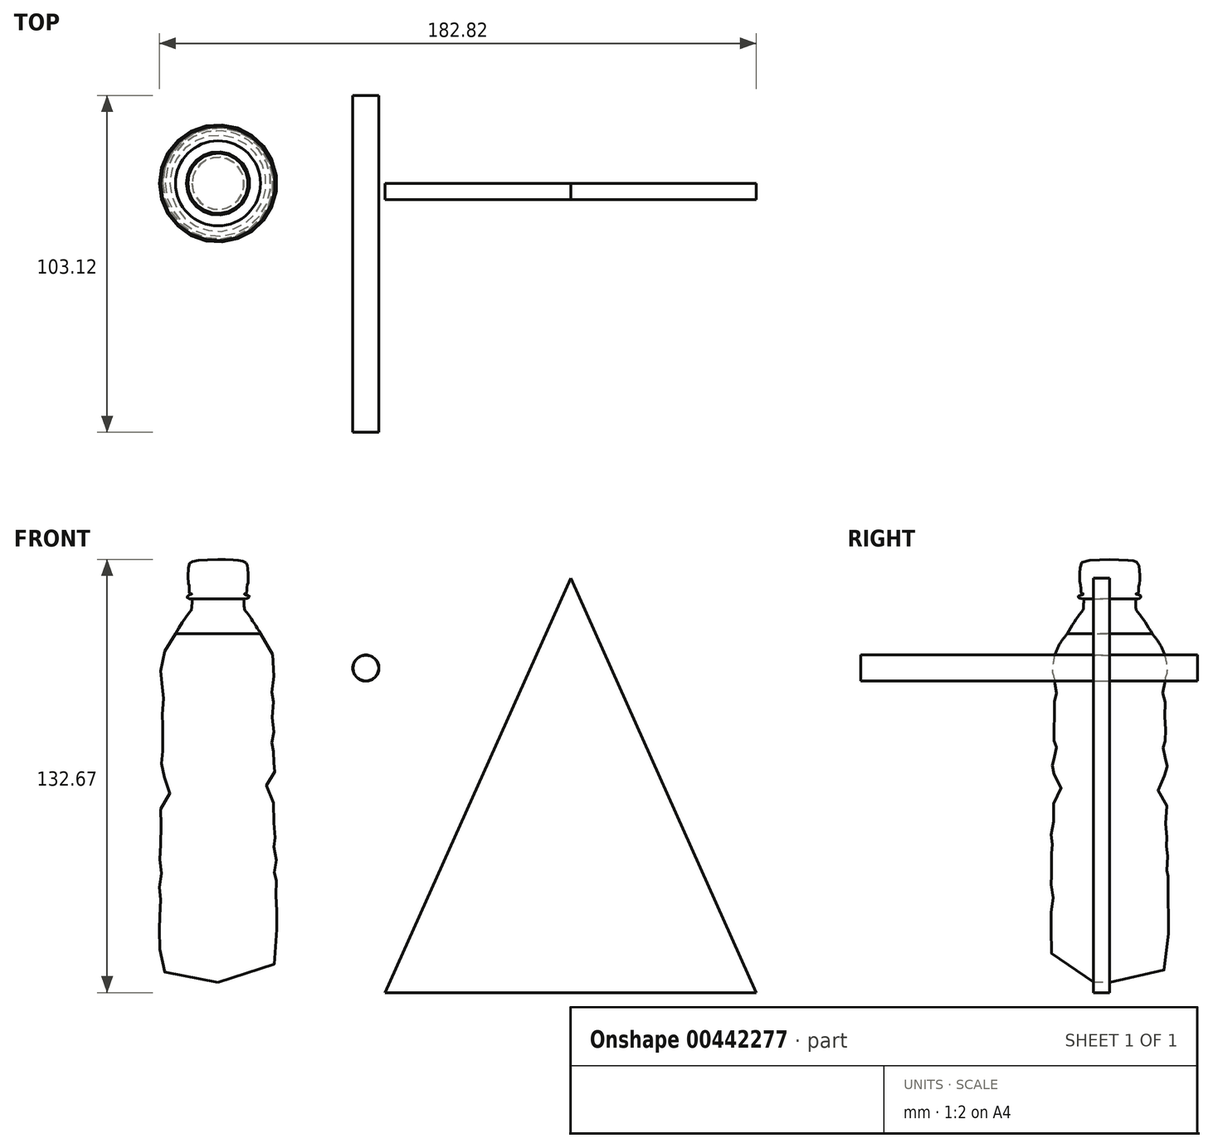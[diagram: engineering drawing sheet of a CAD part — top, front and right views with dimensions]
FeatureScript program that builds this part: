
annotation { "Feature Type Name" : "Feature", "Feature Type Description" : "" }
export const myFeature = defineFeature(function(context is Context, id is Id, definition is map)
    precondition{}
    {
        {
            var Q0;
            Q0=qCreatedBy(makeId("Front.planeOp"),FACE);
            var sketch = newSketch(context, id + "F0", { "sketchPlane" : qUnion([Q0])});
            skLineSegment(sketch, "E0", {"start": v(-25.2, -72.37) * mm, "end": v(-25.2, 34.47) * mm});
            skPoint(sketch, "E0.startSnap0", {"position": v(-25.2, -77.68) * mm});
            skLineSegment(sketch, "E1", {"start": v(-25.2, 34.47) * mm, "end": v(-38.23, 34.47) * mm});
            skFitSpline(sketch, "E2", {"points": [v(-38.23, 34.47) * mm, v(-39.29, 33.05) * mm, v(-40.03, 32.06) * mm, v(-41.03, 30.36) * mm, v(-41.81, 28.4) * mm, v(-42.22, 27.1) * mm, v(-42.63, 24.63) * mm, v(-42.75, 23.45) * mm, v(-42.66, 22.2) * mm, v(-42.19, 20.87) * mm, v(-42.19, 19.83) * mm, v(-42.21, 18.8) * mm, v(-42.22, 18.02) * mm, v(-42.18, 17.28) * mm, v(-41.85, 16.73) * mm, v(-41.48, 16.36) * mm, v(-41.4, 15.76) * mm, v(-41.53, 15.28) * mm, v(-41.82, 14.68) * mm, v(-42.06, 14.12) * mm, v(-42.26, 12.97) * mm, v(-42.27, 11.72) * mm, v(-42.26, 10.27) * mm, v(-42.17, 9.37) * mm, v(-41.66, 8.62) * mm, v(-41.4, 8.31) * mm, v(-41.4, 7.93) * mm, v(-41.57, 7.47) * mm, v(-41.9, 6.95) * mm, v(-42.15, 6.44) * mm, v(-42.28, 5.8) * mm, v(-42.32, 4.81) * mm, v(-42.34, 2.78) * mm, v(-42.31, 1.99) * mm, v(-42.14, 1.46) * mm, v(-41.78, 1.06) * mm, v(-41.47, 0.82) * mm, v(-41.4, 0.2) * mm, v(-41.52, -0.38) * mm, v(-41.74, -0.69) * mm, v(-42.03, -1.2) * mm, v(-42.13, -1.63) * mm, v(-42.17, -3.16) * mm, v(-42.16, -4.22) * mm, v(-42.16, -4.8) * mm, v(-42.1, -5.02) * mm, v(-42.17, -5.09) * mm, v(-42.4, -5.21) * mm, v(-42.62, -5.47) * mm, v(-42.75, -5.84) * mm, v(-42.86, -6.83) * mm, v(-42.64, -7.82) * mm, v(-42.26, -8.67) * mm, v(-41.4, -9.87) * mm, v(-40.5, -10.8) * mm, v(-40.12, -11.4) * mm, v(-40.04, -13.33) * mm, v(-39.95, -14.61) * mm, v(-40.42, -15.47) * mm, v(-42.14, -17.35) * mm, v(-42.63, -18.26) * mm, v(-42.8, -19.17) * mm, v(-42.93, -20.81) * mm, v(-42.87, -22.15) * mm, v(-42.38, -22.96) * mm, v(-42.38, -23.78) * mm, v(-42.8, -24.45) * mm, v(-42.95, -25.01) * mm, v(-43.05, -27.48) * mm, v(-43.05, -29.64) * mm, v(-42.59, -30.46) * mm, v(-42.28, -31.08) * mm, v(-42.64, -31.44) * mm, v(-43, -32.05) * mm, v(-43, -32.77) * mm, v(-43, -35.03) * mm, v(-43.02, -36.47) * mm, v(-43.05, -37.46) * mm, v(-42.88, -37.98) * mm, v(-42.6, -38.38) * mm, v(-42.48, -38.88) * mm, v(-42.81, -39.23) * mm, v(-43.05, -39.76) * mm, v(-43.1, -40.23) * mm, v(-43.12, -41.3) * mm, v(-43.1, -42.54) * mm, v(-43.1, -43.85) * mm, v(-43.06, -44.91) * mm, v(-43.06, -45.4) * mm, v(-42.83, -45.92) * mm, v(-42.58, -46.35) * mm, v(-42.58, -46.7) * mm, v(-42.78, -47.07) * mm, v(-43.06, -47.46) * mm, v(-43.16, -48.33) * mm, v(-43.2, -49.75) * mm, v(-43.18, -50.24) * mm, v(-43.05, -53.08) * mm, v(-42.97, -53.4) * mm, v(-42.7, -53.84) * mm, v(-42.53, -54.3) * mm, v(-42.9, -54.83) * mm, v(-43.15, -55.49) * mm, v(-43.1, -56.88) * mm, v(-43.1, -58.32) * mm, v(-43.03, -60.03) * mm, v(-43.03, -61.32) * mm, v(-42.9, -64.36) * mm, v(-42.45, -66.76) * mm, v(-41.9, -68.07) * mm, v(-40.25, -70.54) * mm, v(-25.2, -72.37) * mm, v(-24.6, -72.37) * mm], "startDerivative": vector(-93.13, -125.53) * mm, "endDerivative": vector(41.9, 0.83) * mm});
            skLineSegment(sketch, "E3", {"start": v(-25.2, 34.47) * mm, "end": v(-25.2, 57.15) * mm});
            skFitSpline(sketch, "E4", {"points": [v(-38.23, 34.47) * mm, v(-36.3, 37.57) * mm, v(-34.36, 40.4) * mm, v(-33.46, 41.5) * mm, v(-33.27, 41.9) * mm, v(-33.18, 43.78) * mm, v(-33.18, 45.09) * mm, v(-33.3, 45.07) * mm, v(-33.67, 45.08) * mm, v(-34.52, 45.38) * mm, v(-34.85, 45.92) * mm, v(-33.23, 46.52) * mm, v(-33.37, 46.65) * mm, v(-33.93, 46.87) * mm, v(-34.01, 47.04) * mm, v(-34.07, 48.84) * mm, v(-34.13, 49.36) * mm, v(-34.34, 49.8) * mm, v(-34.15, 55.18) * mm, v(-33.7, 56.18) * mm, v(-32.53, 56.68) * mm, v(-25.2, 57.15) * mm], "startDerivative": vector(23.47, 38.14) * mm, "endDerivative": vector(77.4, 2.12) * mm});
            skLineSegment(sketch, "E5", {"start": v(-33.23, 46.52) * mm, "end": v(-28.15, 57.07) * mm, "construction": true});
            skSolve(sketch);
        }
        {
            var Q0;
            {var subQ0=sQuery(id+"F0.wireOp",EDGE,"E0");Q0=makeQuery(id+"F0.imprint","IMPRINT",FACE,{"disambiguationData":[TD([[makeQuery(id+"F0.imprint","IMPRINT",EDGE,{"derivedFrom":subQ0}),1.0]])]});}
            var Q1;
            Q1=makeQuery(id+"F0.imprint","IMPRINT",FACE,{"disambiguationData":[TD([[makeQuery(id+"F0.imprint","IMPRINT",EDGE,{"derivedFrom":sQuery(id+"F0.wireOp",EDGE,"E1")}),-1.0]])]});
            var Q2;
            Q2=sQuery(id+"F0.wireOp",EDGE,"E0");
            revolve(context, id + "F1", {"entities" : qUnion([Q0, Q1]), "axis" : qUnion([Q2]), "revolveType" : RevolveType.FULL});
        }
        {
            var Q0;
            Q0=qCreatedBy(makeId("Front.planeOp"),FACE);
            var sketch = newSketch(context, id + "F2", { "sketchPlane" : qUnion([Q0])});
            skCircle(sketch, "E6", {"center": v(20.06, 23.89) * mm, "radius": 4 * mm});
            skCircle(sketch, "E7", {"center": v(20.06, 23.89) * mm, "radius": 3.92 * mm});
            skSolve(sketch);
        }
        {
            var Q0;
            Q0 = qSketchRegion(id + "F2", true);
            extrude(context, id + "F3", {"entities" : qUnion([Q0]), "depth" : 76.2 * mm, "hasSecondDirection" : true, "secondDirectionOppositeDirection" : true, "secondDirectionDepth" : 26.92 * mm});
        }
        {
            var Q0;
            Q0=qCreatedBy(makeId("Front.planeOp"),FACE);
            var sketch = newSketch(context, id + "F4", { "sketchPlane" : qUnion([Q0])});
            skLineSegment(sketch, "E8", {"start": v(139.62, -75.52) * mm, "end": v(25.95, -75.52) * mm});
            skLineSegment(sketch, "E9", {"start": v(25.95, -75.52) * mm, "end": v(82.78, 51.48) * mm});
            skPoint(sketch, "E9.endSnap0", {"position": v(82.78, -75.52) * mm});
            skLineSegment(sketch, "E10", {"start": v(82.78, 51.48) * mm, "end": v(139.62, -75.52) * mm});
            skSolve(sketch);
        }
        {
            var Q0;
            Q0=makeQuery(id+"F4.imprint","IMPRINT",FACE,{"disambiguationData":[TD([[makeQuery(id+"F4.imprint","IMPRINT",EDGE,{"derivedFrom":sQuery(id+"F4.wireOp",EDGE,"E8")}),-1.0]])]});
            extrude(context, id + "F5", {"entities" : qUnion([Q0]), "depth" : 5 * mm});
        }
    });
